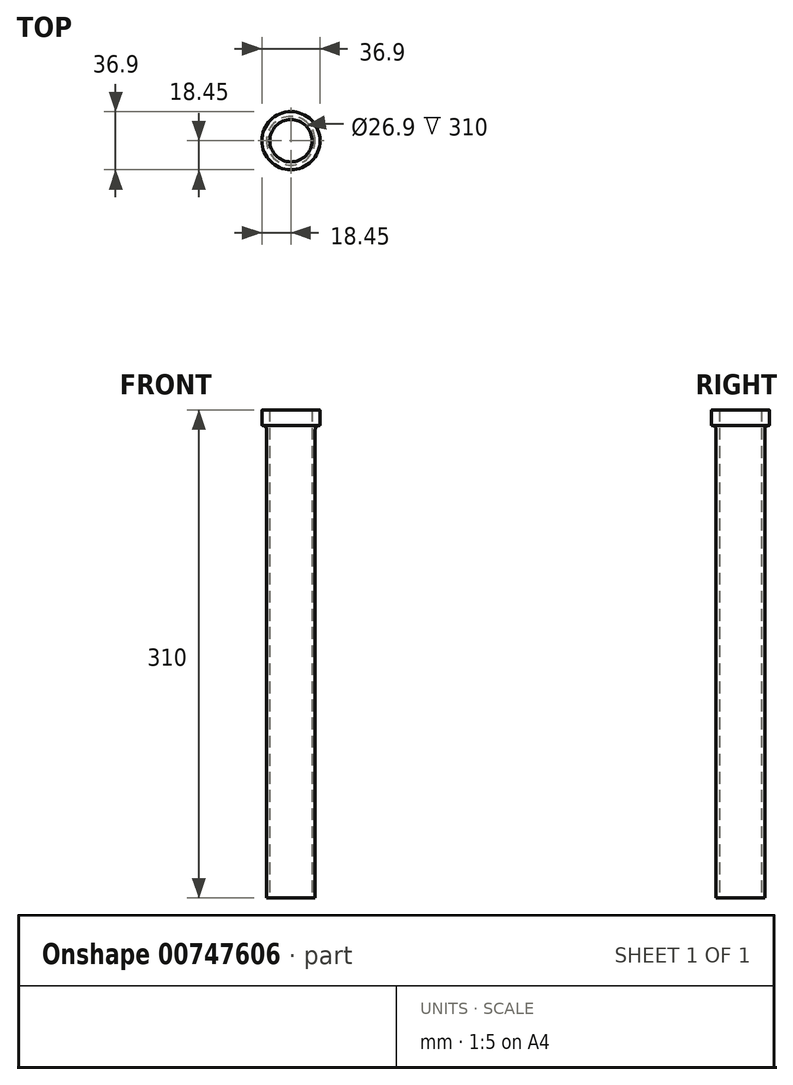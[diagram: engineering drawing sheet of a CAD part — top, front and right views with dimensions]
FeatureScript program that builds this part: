
annotation { "Feature Type Name" : "Feature", "Feature Type Description" : "" }
export const myFeature = defineFeature(function(context is Context, id is Id, definition is map)
    precondition{}
    {
        {
            var Q0;
            Q0=qCreatedBy(makeId("Front.planeOp"),FACE);
            var sketch = newSketch(context, id + "F0", { "sketchPlane" : qUnion([Q0])});
            skLineSegment(sketch, "E0", {"start": v(-13.45, 0) * mm, "end": v(-13.45, 300) * mm});
            skLineSegment(sketch, "E1", {"start": v(-13.45, 0) * mm, "end": v(-15.45, 0) * mm});
            skLineSegment(sketch, "E2", {"start": v(-15.45, 0) * mm, "end": v(-15.45, 297.5) * mm});
            skLineSegment(sketch, "E3", {"start": v(-17.95, 300) * mm, "end": v(-17.95, 300) * mm});
            skLineSegment(sketch, "E4", {"start": v(-18.45, 300.5) * mm, "end": v(-18.45, 309.5) * mm});
            skLineSegment(sketch, "E5", {"start": v(-17.95, 310) * mm, "end": v(-13.45, 310) * mm});
            skLineSegment(sketch, "E6", {"start": v(-13.45, 310) * mm, "end": v(-13.45, 300) * mm});
            skLineSegment(sketch, "E7", {"start": v(0, 0) * mm, "end": v(0, 85.25) * mm, "construction": true});
            skPoint(sketch, "E8.visualSharp", {"position": v(-15.45, 300) * mm});
            skArc(sketch, "E8.filletArc", {"start": v(-15.45, 297.5) * mm, "mid": v(-16.18, 299.27) * mm, "end": v(-17.95, 300) * mm});
            skPoint(sketch, "E9.visualSharp", {"position": v(-18.45, 300) * mm});
            skArc(sketch, "E9.filletArc", {"start": v(-18.45, 300.5) * mm, "mid": v(-18.3, 300.15) * mm, "end": v(-17.95, 300) * mm});
            skPoint(sketch, "E10.visualSharp", {"position": v(-18.45, 310) * mm});
            skArc(sketch, "E10.filletArc", {"start": v(-17.95, 310) * mm, "mid": v(-18.3, 309.85) * mm, "end": v(-18.45, 309.5) * mm});
            skSolve(sketch);
        }
        {
            var Q0;
            Q0=makeQuery(id+"F0.imprint","IMPRINT",FACE,{"disambiguationData":[TD([[makeQuery(id+"F0.imprint","IMPRINT",EDGE,{"derivedFrom":sQuery(id+"F0.wireOp",EDGE,"E0")}),1.0]])]});
            var Q1;
            Q1=sQuery(id+"F0.wireOp",EDGE,"E7");
            revolve(context, id + "F1", {"surfaceOperationType" : NewSurfaceOperationType.NEW, "entities" : qUnion([Q0]), "axis" : qUnion([Q1]), "revolveType" : RevolveType.FULL});
        }
    });
